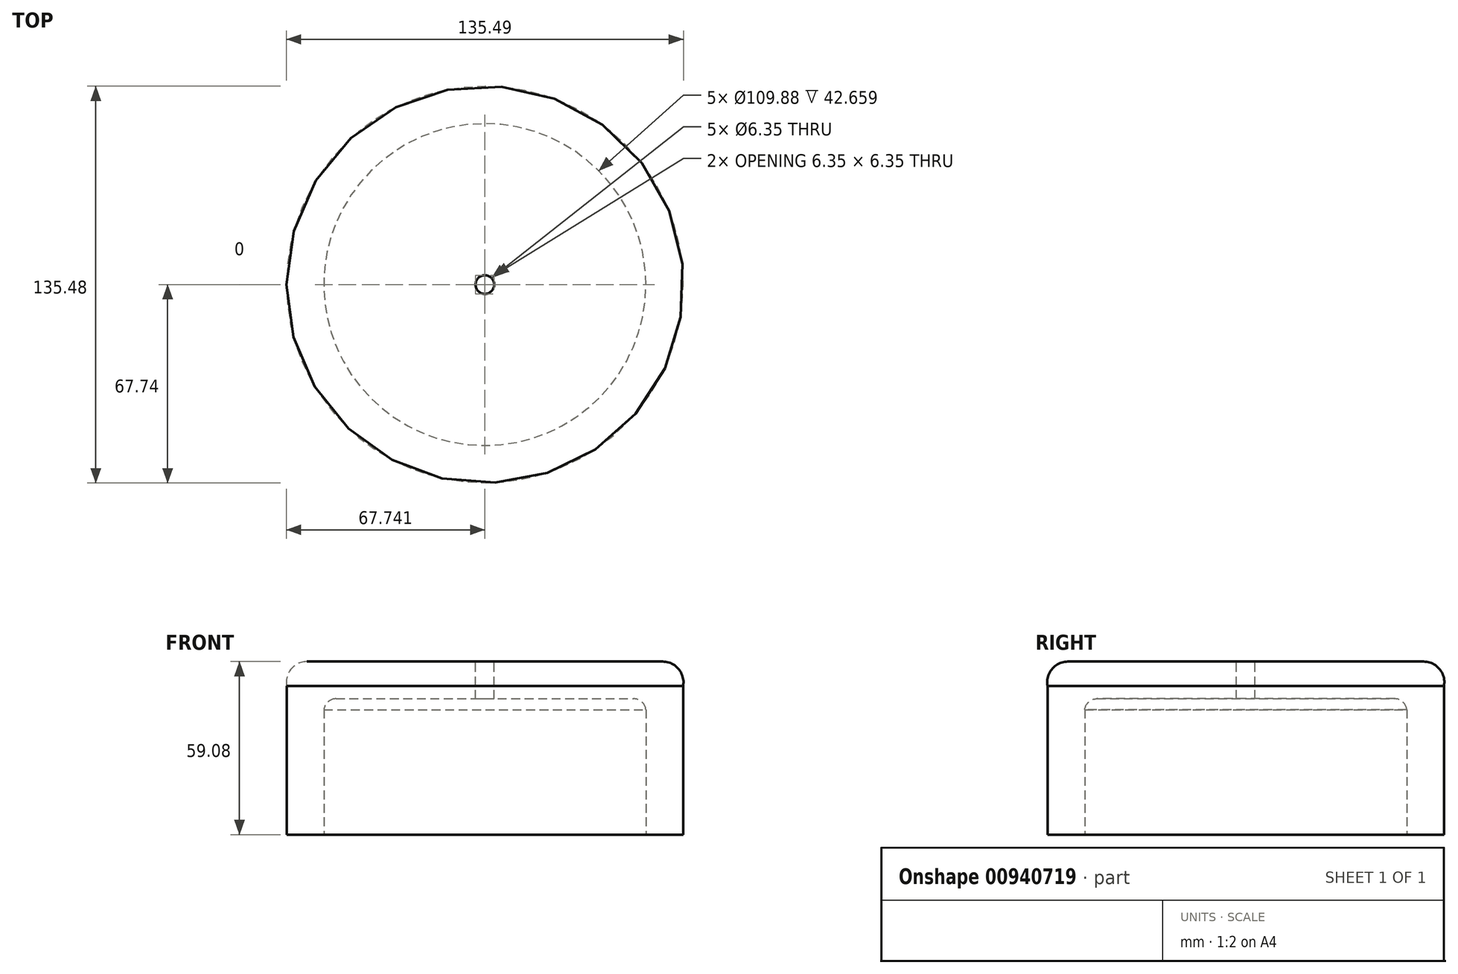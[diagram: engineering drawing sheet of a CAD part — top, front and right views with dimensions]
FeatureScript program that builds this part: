
annotation { "Feature Type Name" : "Feature", "Feature Type Description" : "" }
export const myFeature = defineFeature(function(context is Context, id is Id, definition is map)
    precondition{}
    {
        {
            var Q0;
            Q0=qCreatedBy(makeId("Front.planeOp"),FACE);
            var sketch = newSketch(context, id + "F0", { "sketchPlane" : qUnion([Q0])});
            skLineSegment(sketch, "E0", {"start": v(-71.57, 43.61) * mm, "end": v(-20.77, 43.61) * mm});
            skLineSegment(sketch, "E1", {"start": v(-71.57, 43.61) * mm, "end": v(-71.57, 56.31) * mm});
            skLineSegment(sketch, "E2", {"start": v(-71.57, 56.31) * mm, "end": v(-10.9, 56.31) * mm});
            skArc(sketch, "E3", {"start": v(-3.93, 48.03) * mm, "mid": v(-5.48, 53.8) * mm, "end": v(-10.9, 56.31) * mm});
            skLineSegment(sketch, "E4", {"start": v(-3.93, 48.03) * mm, "end": v(-3.93, -2.77) * mm});
            skLineSegment(sketch, "E5", {"start": v(-3.93, -2.77) * mm, "end": v(-16.63, -2.77) * mm});
            skArc(sketch, "E6", {"start": v(-16.63, 39.89) * mm, "mid": v(-17.99, 42.54) * mm, "end": v(-20.77, 43.61) * mm});
            skLineSegment(sketch, "E7", {"start": v(-16.63, 39.89) * mm, "end": v(-16.63, -2.77) * mm});
            skPoint(sketch, "E8.orphan", {"position": v(-20.77, -2.77) * mm});
            skSolve(sketch);
        }
        {
            var Q0;
            Q0=makeQuery(id+"F0.imprint","IMPRINT",FACE,{"disambiguationData":[TD([[makeQuery(id+"F0.imprint","IMPRINT",EDGE,{"derivedFrom":sQuery(id+"F0.wireOp",EDGE,"E0")}),1.0]])]});
            var Q1;
            Q1=sQuery(id+"F0.wireOp",EDGE,"E1");
            revolve(context, id + "F1", {"surfaceOperationType" : NewSurfaceOperationType.NEW, "entities" : qUnion([Q0]), "axis" : qUnion([Q1]), "revolveType" : RevolveType.FULL});
        }
        {
            var Q0;
            Q0=makeQuery(id+"F1.opRevolve","SWEPT_FACE",FACE,{"disambiguationData":[OSD([sQuery(id+"F0.wireOp",EDGE,"E2")])]});
            var sketch = newSketch(context, id + "F2", { "sketchPlane" : qUnion([Q0])});
            skPoint(sketch, "E9.0", {"position": v(-71.57, 0) * mm});
            skCircle(sketch, "E10", {"center": v(-71.57, 0) * mm, "radius": 3.18 * mm});
            skSolve(sketch);
        }
        {
            var Q0;
            Q0=makeQuery(id+"F2.imprint","IMPRINT",FACE,{"disambiguationData":[TD([[makeQuery(id+"F2.imprint","IMPRINT",EDGE,{"derivedFrom":sQuery(id+"F2.wireOp",EDGE,"E10")}),1.0]])]});
            extrude(context, id + "F3", {"entities" : qUnion([Q0]), "operationType" : NewBodyOperationType.REMOVE, "oppositeDirection" : true, "depth" : 25.4 * mm, "offsetDistance" : 25.4 * mm});
        }
    });
